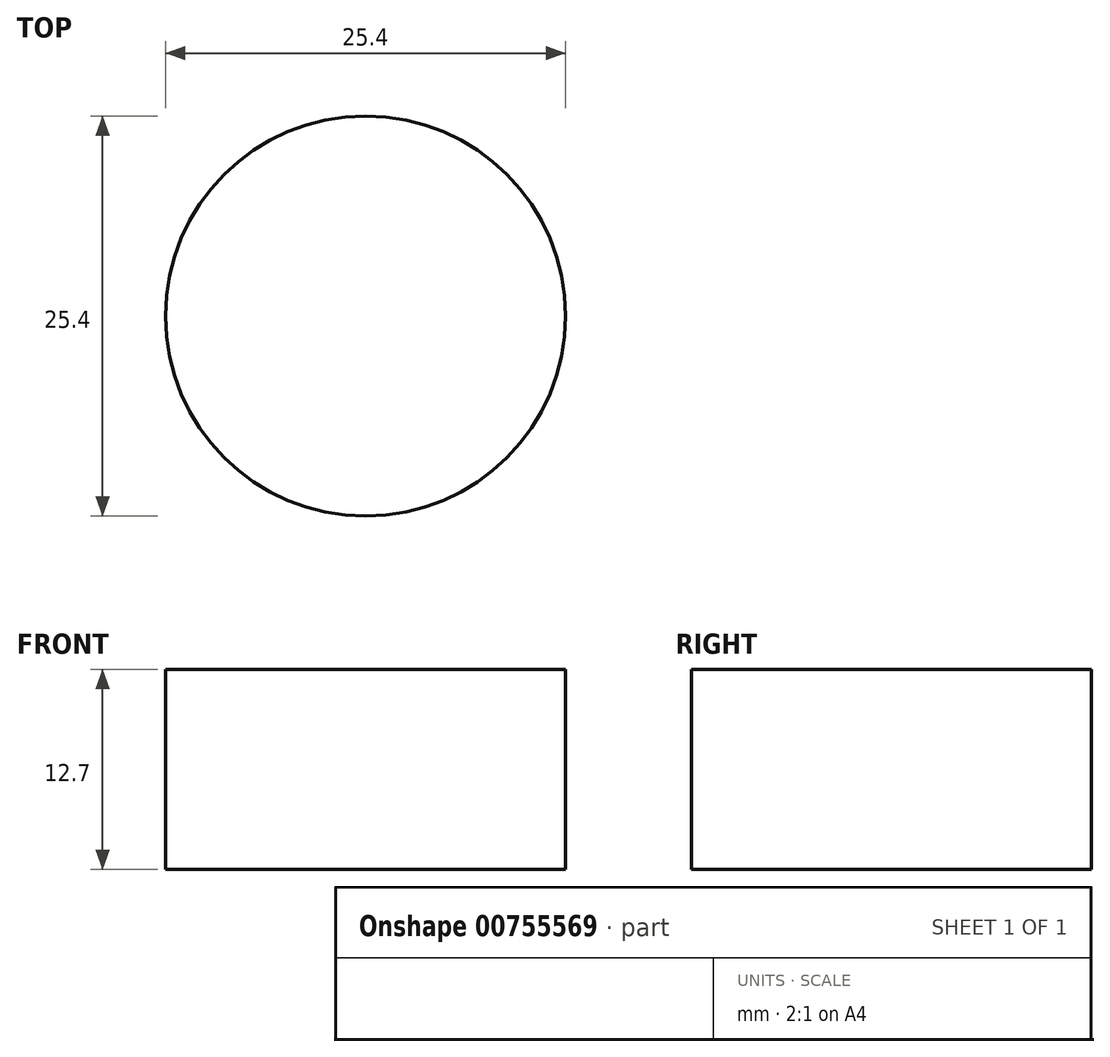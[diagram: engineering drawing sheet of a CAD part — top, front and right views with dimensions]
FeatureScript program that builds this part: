
annotation { "Feature Type Name" : "Feature", "Feature Type Description" : "" }
export const myFeature = defineFeature(function(context is Context, id is Id, definition is map)
    precondition{}
    {
        {
            var Q0;
            Q0=qCreatedBy(makeId("Top.planeOp"),FACE);
            var sketch = newSketch(context, id + "F0", { "sketchPlane" : qUnion([Q0])});
            skCircle(sketch, "E0", {"center": v(0, 0) * mm, "radius": 12.7 * mm});
            skSolve(sketch);
        }
        {
            var Q0;
            Q0=makeQuery(id+"F0.imprint","IMPRINT",FACE,{"disambiguationData":[TD([[makeQuery(id+"F0.imprint","IMPRINT",EDGE,{"derivedFrom":sQuery(id+"F0.wireOp",EDGE,"E0")}),1.0]])]});
            extrude(context, id + "F1", {"entities" : qUnion([Q0]), "depth" : 12.7 * mm, "offsetDistance" : 25.4 * mm});
        }
    });
